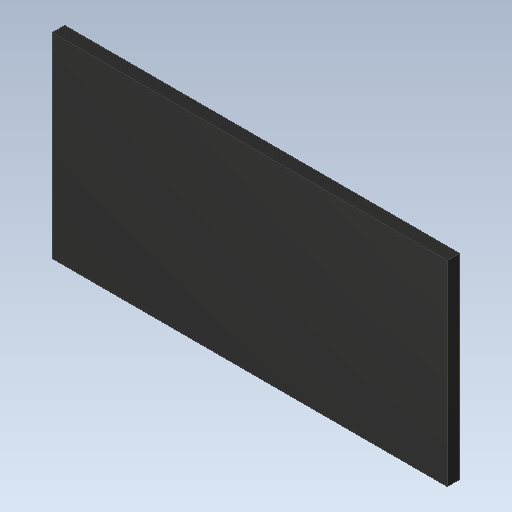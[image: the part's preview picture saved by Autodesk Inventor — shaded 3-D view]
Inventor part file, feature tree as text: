
AUTODESK INVENTOR PART (.ipt)
format: ipt  version: 2023 (Build 270158000, 158)  size: 92,160 bytes
history: imported  units: in
note: dims shown in document units (in); Inventor stores cm internally (conversion verified against a paired STEP export)
features: imported_body x1
ambient origin geometry x8: Origin, YZ Plane, XZ Plane, XY Plane, X Axis, Y Axis, Z Axis, Center Point
bodies: Solid1 (imported_parasolid), Body1 (imported_parasolid)
feature tree (1):
  imported_body  NMx_Import_Brep_tag  [imported B-rep: ~6 faces, bbox_mm=[3.227, 1.6, 0.1]]
